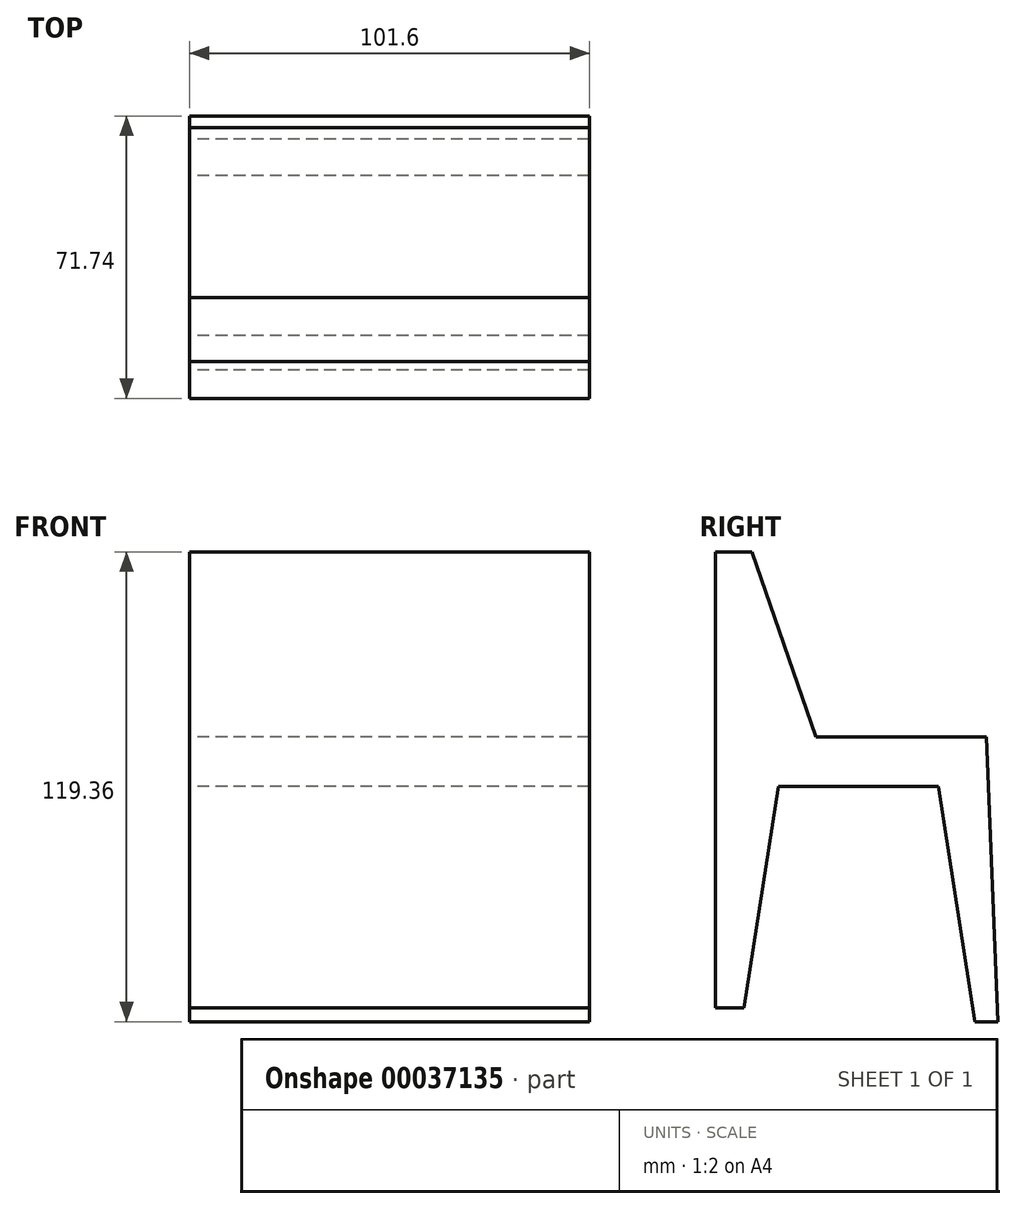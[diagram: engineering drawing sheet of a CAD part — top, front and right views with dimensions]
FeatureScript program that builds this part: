
annotation { "Feature Type Name" : "Feature", "Feature Type Description" : "" }
export const myFeature = defineFeature(function(context is Context, id is Id, definition is map)
    precondition{}
    {
        {
            var Q0;
            Q0=qCreatedBy(makeId("Right.planeOp"),FACE);
            var sketch = newSketch(context, id + "F0", { "sketchPlane" : qUnion([Q0])});
            skLineSegment(sketch, "E0", {"start": v(-54.3, 57.36) * mm, "end": v(-54.3, -58.52) * mm});
            skLineSegment(sketch, "E1", {"start": v(-54.3, -58.52) * mm, "end": v(-47.05, -58.52) * mm});
            skLineSegment(sketch, "E2", {"start": v(-47.05, -58.52) * mm, "end": v(-38.34, -2.18) * mm});
            skLineSegment(sketch, "E3", {"start": v(-38.34, -2.18) * mm, "end": v(2.32, -2.18) * mm});
            skLineSegment(sketch, "E4", {"start": v(2.32, -2.18) * mm, "end": v(11.62, -62) * mm});
            skLineSegment(sketch, "E5", {"start": v(11.62, -62) * mm, "end": v(17.43, -62) * mm});
            skLineSegment(sketch, "E6", {"start": v(17.43, -62) * mm, "end": v(14.52, 10.3) * mm});
            skPoint(sketch, "E6.endSnap0", {"position": v(14.52, -62) * mm});
            skLineSegment(sketch, "E7", {"start": v(14.52, 10.3) * mm, "end": v(-28.75, 10.3) * mm});
            skLineSegment(sketch, "E8", {"start": v(-28.75, 10.3) * mm, "end": v(-45.01, 57.36) * mm});
            skLineSegment(sketch, "E9", {"start": v(-45.01, 57.36) * mm, "end": v(-54.3, 57.36) * mm});
            skSolve(sketch);
        }
        {
            var Q0;
            Q0=makeQuery(id+"F0.imprint","IMPRINT",FACE,{"disambiguationData":[TD([[makeQuery(id+"F0.imprint","IMPRINT",EDGE,{"derivedFrom":sQuery(id+"F0.wireOp",EDGE,"E0")}),1.0]])]});
            extrude(context, id + "F1", {"entities" : qUnion([Q0]), "depth" : 101.6 * mm});
        }
    });
